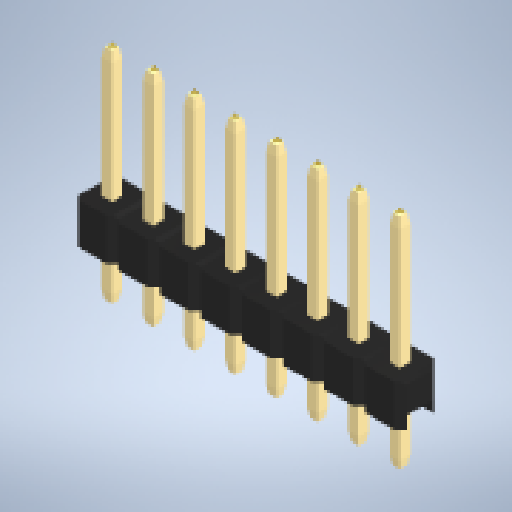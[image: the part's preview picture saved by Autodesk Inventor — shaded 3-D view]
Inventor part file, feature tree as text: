
AUTODESK INVENTOR PART (.ipt)
format: ipt  version: 2023.1 (Build 271208000, 208)  size: 331,264 bytes
history: native  units: in
note: dims shown in document units (in); Inventor stores cm internally (conversion verified against a paired STEP export)
features: other x8, chamfer x1, boolean_combine x1
ambient origin geometry x8: Origin, YZ Plane, XZ Plane, XY Plane, X Axis, Y Axis, Z Axis, Center Point
bodies: Solid1 (feature_tree), Solid2 (feature_tree), Solid3 (feature_tree), Solid4 (feature_tree), Solid5 (feature_tree), Solid6 (feature_tree), Solid7 (feature_tree), Solid8 (feature_tree), Solid9 (feature_tree)
feature tree (10):
  other  "Work Point5"
  chamfer  "Chamfer3"  [1 undecoded]
  other  "LPattern1[1]"
  other  "LPattern1[2]"
  other  "LPattern1[3]"
  other  "LPattern1[4]"
  other  "LPattern1[5]"
  other  "LPattern1[6]"
  other  "LPattern1[7]"
  boolean_combine  "Combine1"
note: 1 required parameter value undecoded (feature->parameter linkage not recoverable at this tier; creation-order binding heuristic only, values carry confidence <= 0.55)
